# Revit family: Cutter_K-52_1_GENERADO
name_source: partatom
category: Equipos especializados
units: mm (PartAtom-declared; Revit-internal decimal feet)

## family parameters
Compartido = No
Corte con vacíos al cargar = No
Cota de conector redondo = Diámetro de uso
Número OmniClass = 23.21.21.31.15
Punto de cálculo de habitación = No
Se basa en plano de trabajo = No
Siempre vertical = Sí
Tipo de pieza = Normal

## types (1)
- Cutter K-52 400/50/3N
    Comentarios de tipo = Bowl capacity: 5.5 lt. 2-speed.
    Cycle = 50 Hz
    Depth = 387 mm  [stored 1.26969 ft]
    Descripción = Cutter K-52 400/50/3N
    Electric Connection Type = 3P+G
    Elevación por defecto = 0 mm  [stored 0 ft]
    FL Amps = 3 A
    Fabricante = SAMMIC S.L.
    Foodservice Equipment Identifier = Sí
    HP = 1.21
    Height = 439 mm  [stored 1.44029 ft]
    Modelo = 1050832
    Phase = 3
    Revision Code = 1
    Specification by Manufacturer = To cut, grind, mix and knead any food in seconds.
    URL = https://www.sammic.com
    URL Cutsheet = http://www.sammic.com
    Volts = 400 V
    Watts = 900 W
    Weight in Pounds = 47.6
    Width = 286 mm  [stored 0.93832 ft]

note: [stored X ft] marks values corroborated as IEEE doubles in the binary element streams (Revit-internal decimal feet)

## geometry (parser evidence)
native form markers: Revolve x5
no freeform markers — native parametric forms only
